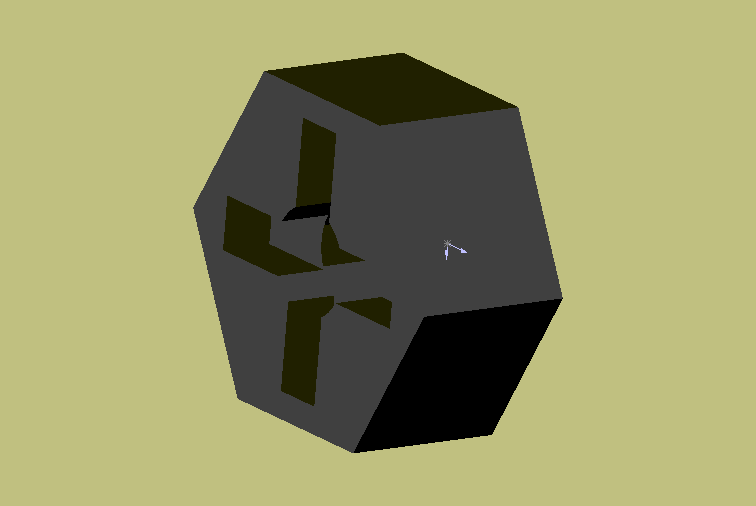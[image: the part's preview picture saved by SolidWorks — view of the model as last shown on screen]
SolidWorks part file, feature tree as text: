
SOLIDWORKS PART (.sldprt)
format: sldprt  version: not decoded by parser v0  size: 112,128 bytes
history: native  units: mm
features: plane x3, sketch x3, cut_extrude x2, material x1, extrude x1 (+8 scaffold rows collapsed)
feature tree (18):
  scaffold x8  (default folders/planes/origin — collapsed)
  material  "Matériau <non spécifié>"
  plane  "Plane1"
  plane  "Plane2"
  plane  "Plane3"
  sketch  "Esquisse1"  dims[D2=4.0mm D1=12.0mm]
  extrude  "Base-Extrusion"  Depth=6mm
  sketch  "Esquisse2"  dims[D1=5.0mm D2=2.0mm]
  cut_extrude  "Enlèv. mat.-Extru.1"  Depth=2mm
  sketch  "Esquisse3"
  cut_extrude  "Enlèv. mat.-Extru.2"  Depth=2mm
decode coverage: 5 of 6 modeling features carry decoded parameters
note: suppression state not decoded; provenance and decode notes live in map.json
